# Revit family: SW04 BRÆDDER - RUHØVLET
name_source: partatom
category: Detail Items
units: mm (PartAtom-declared; Revit-internal decimal feet)

## family parameters
Rotate with component = No
Section Shape = Not Defined
Shared = No

## types (10) — shared parameters
URL = www.superwood.dk

## per-type parameters (varying)
| type | b | d |
| SW04 BRÆDDER - 27x45mm | 27 mm  [stored 0.0885827 ft] | 45 mm  [stored 0.147638 ft] |
| SW04 BRÆDDER - 27x70mm | 27 mm  [stored 0.0885827 ft] | 70 mm  [stored 0.229659 ft] |
| SW04 BRÆDDER - 21x70mm | 21 mm  [stored 0.0688976 ft] | 70 mm  [stored 0.229659 ft] |
| SW04 BRÆDDER - 21x45mm | 21 mm  [stored 0.0688976 ft] | 45 mm  [stored 0.147638 ft] |
| SW04 BRÆDDER - 27x95mm | 27 mm  [stored 0.0885827 ft] | 95 mm |
| SW04 BRÆDDER - 27x145mm | 27 mm  [stored 0.0885827 ft] | 145 mm  [stored 0.475722 ft] |
| SW04 BRÆDDER - 27x120mm | 27 mm  [stored 0.0885827 ft] | 120 mm  [stored 0.393701 ft] |
| SW04 BRÆDDER - 21x145mm | 21 mm  [stored 0.0688976 ft] | 145 mm  [stored 0.475722 ft] |
| SW04 BRÆDDER - 21x120mm | 21 mm  [stored 0.0688976 ft] | 120 mm  [stored 0.393701 ft] |
| SW04 BRÆDDER - 21x95mm | 21 mm  [stored 0.0688976 ft] | 95 mm |

note: [stored X ft] marks values corroborated as IEEE doubles in the binary element streams (Revit-internal decimal feet)

## geometry (parser evidence)
native form markers: Sweep x1
no freeform markers — native parametric forms only
